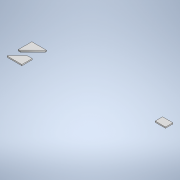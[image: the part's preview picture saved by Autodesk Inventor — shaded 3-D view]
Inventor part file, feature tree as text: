
AUTODESK INVENTOR PART (.ipt)
format: ipt  version: 2022 (Build 260153000, 153)  size: 235,520 bytes
history: native  units: in
note: dims shown in document units (in); Inventor stores cm internally (conversion verified against a paired STEP export)
features: extrude x1, sketch x1
ambient origin geometry x8: Origin, YZ Plane, XZ Plane, XY Plane, X Axis, Y Axis, Z Axis, Center Point
bodies: Body1 (feature_tree)
feature tree (2):
  extrude  "Extrusion2"  Depth=0.1181in
  sketch  "Sketch1"  dims[d0=20.0in d1=12.0in d2=19.685in d3=11.811in d6=2.7559in d7=4.0157in d8=1.1811in d10=3.4252in d11=1.1811in d13=3.4252in d16=135.0deg d17=135.0deg d18=0.5512in d19=0.5512in d20=0.5906in d21=0.7874in d22=0.5906in d23=0.5906in d24=0.7874in d25=0.5906in d26=0.5906in d27=0.4331in d28=0.5906in d29=0.8268in d30=0.8268in d31=0.5512in d32=0.7874in d33=0.5906in d34=0.6693in d35=0.7874in d36=0.6693in d38=0.5512in d43=0.0in d45=0.5906in d47=135.0deg d49=0.5906in d51=135.0deg d56=0.7874in d57=45.0deg d58=0.5906in d59=0.5906in d60=0.1181in d61=0.0in d62=45.0deg d63=18.2677in d64=0.5906in d67=5.8268in d68=16.4567in d69=4.0157in d70=0.5512in d71=0.1457in d72=0.1969in d73=0.1969in d74=4.2126in d75=4.2126in d76=4.2126in d77=4.2126in d78=0.3898in d79=0.1161in d80=0.3898in]
